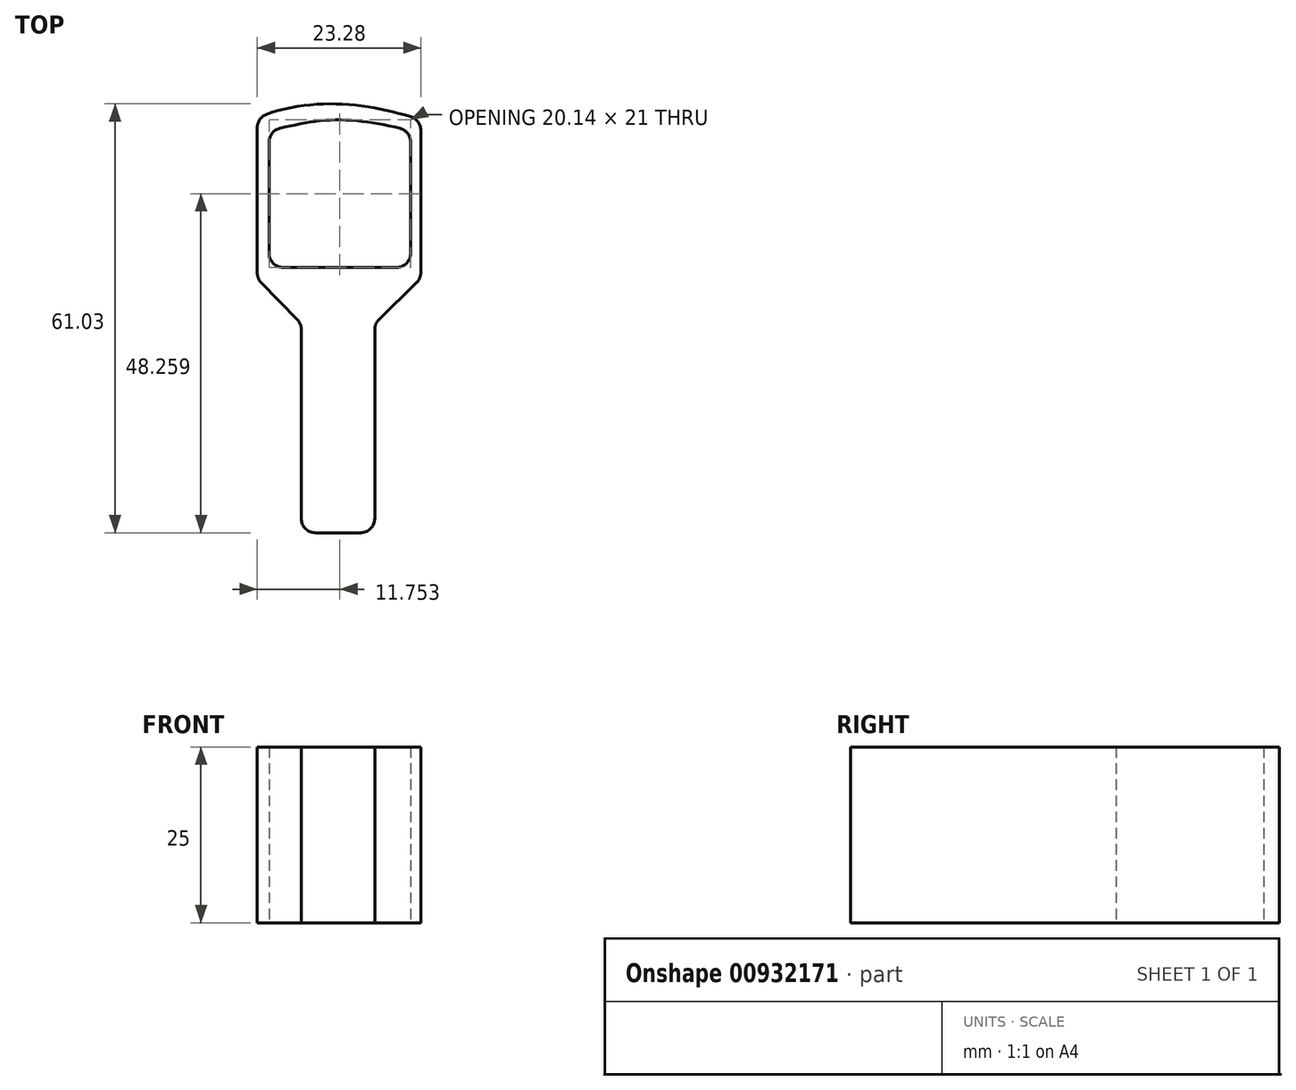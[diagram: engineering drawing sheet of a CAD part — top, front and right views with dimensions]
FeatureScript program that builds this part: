
annotation { "Feature Type Name" : "Feature", "Feature Type Description" : "" }
export const myFeature = defineFeature(function(context is Context, id is Id, definition is map)
    precondition{}
    {
        {
            var Q0;
            Q0=qCreatedBy(makeId("Top.planeOp"),FACE);
            var sketch = newSketch(context, id + "F0", { "sketchPlane" : qUnion([Q0])});
            skLineSegment(sketch, "E0", {"start": v(3.98, 16.84) * mm, "end": v(20.12, 16.84) * mm});
            skLineSegment(sketch, "E1", {"start": v(22.12, 18.84) * mm, "end": v(22.12, 34.7) * mm});
            skLineSegment(sketch, "E2", {"start": v(1.98, 34.7) * mm, "end": v(1.98, 18.84) * mm});
            skPoint(sketch, "E3.visualSharp", {"position": v(1.98, 16.84) * mm});
            skArc(sketch, "E3.filletArc", {"start": v(1.98, 18.84) * mm, "mid": v(2.57, 17.42) * mm, "end": v(3.98, 16.84) * mm});
            skPoint(sketch, "E4.visualSharp", {"position": v(22.12, 16.84) * mm});
            skArc(sketch, "E4.filletArc", {"start": v(20.12, 16.84) * mm, "mid": v(21.53, 17.42) * mm, "end": v(22.12, 18.84) * mm});
            skFitSpline(sketch, "E5", {"points": [v(1.98, 36.28) * mm, v(11.63, 37.84) * mm, v(22.12, 36.28) * mm], "startDerivative": vector(20.51, 4.84) * mm, "endDerivative": vector(19.76, -4.87) * mm});
            skLineSegment(sketch, "E6", {"start": v(6, 9.42) * mm, "end": v(0.87, 14.67) * mm});
            skLineSegment(sketch, "E7", {"start": v(0.3, 16.07) * mm, "end": v(0.3, 36.75) * mm});
            skFitSpline(sketch, "E8", {"points": [v(0.3, 38.1) * mm, v(12.01, 40.1) * mm, v(23.58, 37.83) * mm], "startDerivative": vector(21.36, 9.53) * mm, "endDerivative": vector(23.25, -7.63) * mm});
            skLineSegment(sketch, "E9", {"start": v(23.58, 36.36) * mm, "end": v(23.58, 16.1) * mm});
            skLineSegment(sketch, "E10", {"start": v(22.97, 14.66) * mm, "end": v(17.62, 9.43) * mm});
            skLineSegment(sketch, "E11", {"start": v(6.57, 8.02) * mm, "end": v(6.57, -18.92) * mm});
            skLineSegment(sketch, "E12", {"start": v(8.57, -20.92) * mm, "end": v(15.01, -20.92) * mm});
            skLineSegment(sketch, "E13", {"start": v(17.01, -18.92) * mm, "end": v(17.01, 8) * mm});
            skLineSegment(sketch, "E14", {"start": v(17.01, 6.89) * mm, "end": v(6.57, 6.89) * mm});
            skLineSegment(sketch, "E15", {"start": v(17.01, -4.34) * mm, "end": v(6.57, -4.34) * mm});
            skPoint(sketch, "E16.visualSharp", {"position": v(6.57, -20.92) * mm});
            skArc(sketch, "E16.filletArc", {"start": v(6.57, -18.92) * mm, "mid": v(7.15, -20.34) * mm, "end": v(8.57, -20.92) * mm});
            skPoint(sketch, "E17.visualSharp", {"position": v(17.01, -20.92) * mm});
            skArc(sketch, "E17.filletArc", {"start": v(15.01, -20.92) * mm, "mid": v(16.43, -20.34) * mm, "end": v(17.01, -18.92) * mm});
            skPoint(sketch, "E18.visualSharp", {"position": v(17.01, 8.84) * mm});
            skArc(sketch, "E18.filletArc", {"start": v(17.62, 9.43) * mm, "mid": v(17.17, 8.77) * mm, "end": v(17.01, 8) * mm});
            skPoint(sketch, "E19.visualSharp", {"position": v(23.58, 15.25) * mm});
            skArc(sketch, "E19.filletArc", {"start": v(22.97, 14.66) * mm, "mid": v(23.42, 15.32) * mm, "end": v(23.58, 16.1) * mm});
            skPoint(sketch, "E20.visualSharp", {"position": v(0.3, 15.25) * mm});
            skArc(sketch, "E20.filletArc", {"start": v(0.3, 16.07) * mm, "mid": v(0.44, 15.31) * mm, "end": v(0.87, 14.67) * mm});
            skPoint(sketch, "E21.visualSharp", {"position": v(6.57, 8.84) * mm});
            skArc(sketch, "E21.filletArc", {"start": v(6.57, 8.02) * mm, "mid": v(6.42, 8.78) * mm, "end": v(6, 9.42) * mm});
            skArc(sketch, "E22.filletArc", {"start": v(1.61, 38.63) * mm, "mid": v(0.66, 37.9) * mm, "end": v(0.3, 36.75) * mm});
            skArc(sketch, "E23.filletArc", {"start": v(23.58, 36.36) * mm, "mid": v(23.18, 37.55) * mm, "end": v(22.15, 38.27) * mm});
            skArc(sketch, "E24.filletArc", {"start": v(3.53, 36.64) * mm, "mid": v(2.42, 35.94) * mm, "end": v(1.98, 34.7) * mm});
            skArc(sketch, "E25.filletArc", {"start": v(22.12, 34.7) * mm, "mid": v(21.68, 35.94) * mm, "end": v(20.57, 36.65) * mm});
            skSolve(sketch);
        }
        {
            var Q0;
            Q0=makeQuery(id+"F0.imprint","IMPRINT",FACE,{"disambiguationData":[TD([[makeQuery(id+"F0.imprint","IMPRINT",EDGE,{"derivedFrom":sQuery(id+"F0.wireOp",EDGE,"E0")}),-1.0]])]});
            var Q1;
            {var subQ0=sQuery(id+"F0.wireOp",EDGE,"E14");Q1=makeQuery(id+"F0.imprint","IMPRINT",FACE,{"disambiguationData":[TD([[makeQuery(id+"F0.imprint","IMPRINT",EDGE,{"derivedFrom":subQ0}),1.0]])]});}
            var Q2;
            Q2=makeQuery(id+"F0.imprint","IMPRINT",FACE,{"disambiguationData":[TD([[makeQuery(id+"F0.imprint","IMPRINT",EDGE,{"derivedFrom":sQuery(id+"F0.wireOp",EDGE,"E12")}),1.0]])]});
            extrude(context, id + "F1", {"entities" : qUnion([Q0, Q1, Q2]), "depth" : 25 * mm, "offsetDistance" : 25 * mm});
        }
    });
